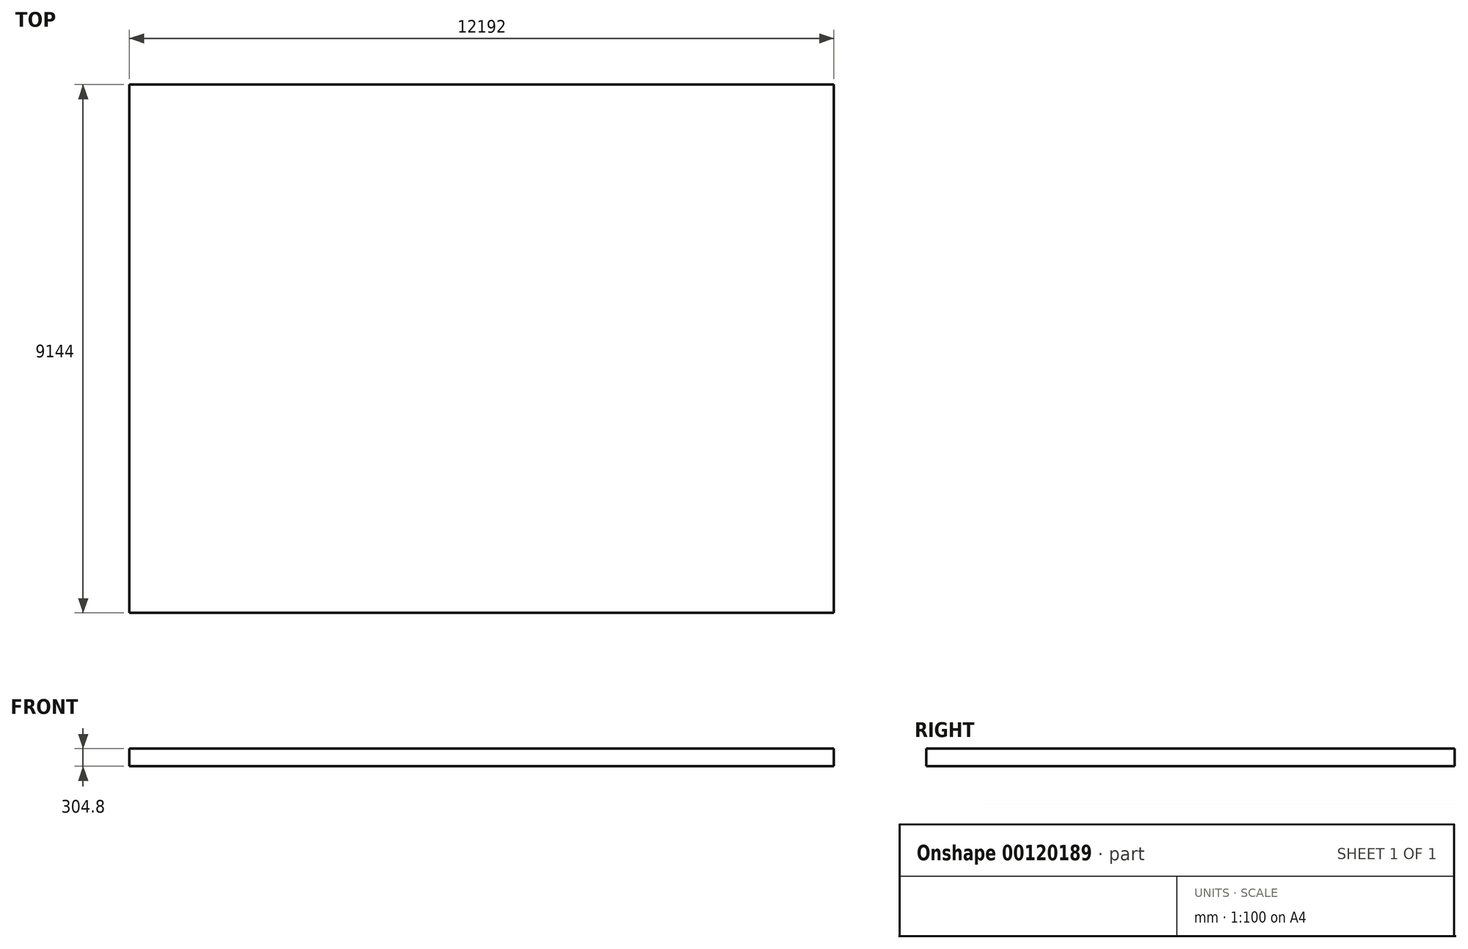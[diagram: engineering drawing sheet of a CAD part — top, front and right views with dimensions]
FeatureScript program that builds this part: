
annotation { "Feature Type Name" : "Feature", "Feature Type Description" : "" }
export const myFeature = defineFeature(function(context is Context, id is Id, definition is map)
    precondition{}
    {
        {
            var Q0;
            Q0=qCreatedBy(makeId("Top.planeOp"),FACE);
            var sketch = newSketch(context, id + "F0", { "sketchPlane" : qUnion([Q0])});
            skLineSegment(sketch, "E0.bottom", {"start": v(-6096, 4572) * mm, "end": v(6096, 4572) * mm});
            skLineSegment(sketch, "E0.top", {"start": v(-6096, -4572) * mm, "end": v(6096, -4572) * mm});
            skLineSegment(sketch, "E0.left", {"start": v(-6096, 4572) * mm, "end": v(-6096, -4572) * mm});
            skLineSegment(sketch, "E0.right", {"start": v(6096, 4572) * mm, "end": v(6096, -4572) * mm});
            skPoint(sketch, "E0.middle", {"position": v(0, 0) * mm});
            skSolve(sketch);
        }
        {
            var Q0;
            Q0 = qSketchRegion(id + "F0", true);
            extrude(context, id + "F1", {"entities" : qUnion([Q0]), "depth" : 304.8 * mm});
        }
    });
